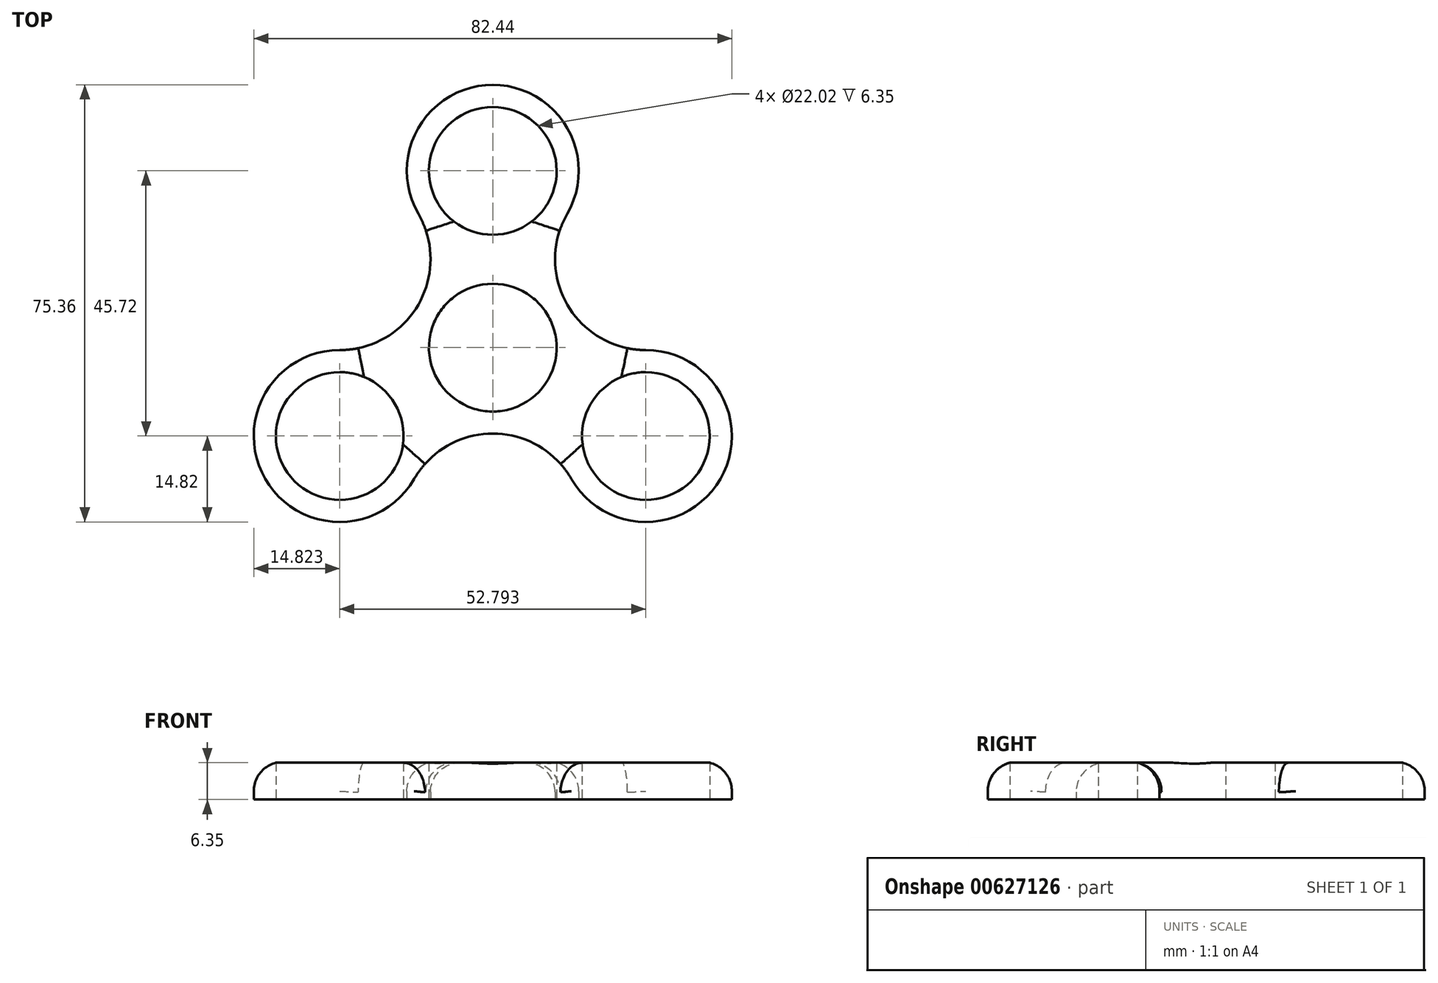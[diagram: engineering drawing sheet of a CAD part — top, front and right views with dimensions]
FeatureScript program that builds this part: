
annotation { "Feature Type Name" : "Feature", "Feature Type Description" : "" }
export const myFeature = defineFeature(function(context is Context, id is Id, definition is map)
    precondition{}
    {
        {
            var Q0;
            Q0=qCreatedBy(makeId("Top.planeOp"),FACE);
            var sketch = newSketch(context, id + "F0", { "sketchPlane" : qUnion([Q0])});
            skCircle(sketch, "E0", {"center": v(0, 0) * mm, "radius": 11.01 * mm});
            skCircle(sketch, "E1", {"center": v(0, 0) * mm, "radius": 14.82 * mm});
            skLineSegment(sketch, "E2", {"start": v(0, 0) * mm, "end": v(0, 30.48) * mm});
            skLineSegment(sketch, "E3", {"start": v(0, 0) * mm, "end": v(26.4, -15.24) * mm});
            skLineSegment(sketch, "E4", {"start": v(0, 0) * mm, "end": v(-26.4, -15.24) * mm});
            skCircle(sketch, "E5", {"center": v(-26.4, -15.24) * mm, "radius": 11.01 * mm});
            skCircle(sketch, "E6", {"center": v(26.4, -15.24) * mm, "radius": 11.01 * mm});
            skCircle(sketch, "E7", {"center": v(0, 30.48) * mm, "radius": 11.01 * mm});
            skCircle(sketch, "E8", {"center": v(0, 30.48) * mm, "radius": 14.82 * mm});
            skCircle(sketch, "E9", {"center": v(26.4, -15.24) * mm, "radius": 14.82 * mm});
            skCircle(sketch, "E10", {"center": v(-26.4, -15.24) * mm, "radius": 14.82 * mm});
            skArc(sketch, "E11", {"start": v(-26.4, -0.42) * mm, "mid": v(-12.84, 7.41) * mm, "end": v(-12.84, 23.07) * mm});
            skArc(sketch, "E12", {"start": v(12.84, 23.07) * mm, "mid": v(12.84, 7.41) * mm, "end": v(26.4, -0.42) * mm});
            skArc(sketch, "E13", {"start": v(13.56, -22.65) * mm, "mid": v(0, -14.82) * mm, "end": v(-13.56, -22.65) * mm});
            skSolve(sketch);
        }
        {
            var Q0;
            Q0 = qSketchRegion(id + "F0", true);
            var Q1;
            {var subQ0=sQuery(id+"F0.wireOp",EDGE,"E4");var subQ1=sQuery(id+"F0.wireOp",EDGE,"E0");var subQ2=makeQuery(id+"F0.imprint","INTERSECT",VERTEX,{"derivedFrom":[subQ1,subQ0]});Q1=makeQuery(id+"F0.imprint","IMPRINT",FACE,{"disambiguationData":[TD([[makeQuery(id+"F0.imprint","IMPRINT",EDGE,{"disambiguationData":[TD([[subQ2,1.0]])],"derivedFrom":subQ1}),-1.0]])]});}
            var Q2;
            {var subQ0=sQuery(id+"F0.wireOp",EDGE,"E4");var subQ1=sQuery(id+"F0.wireOp",EDGE,"E0");var subQ2=makeQuery(id+"F0.imprint","INTERSECT",VERTEX,{"derivedFrom":[subQ1,subQ0]});Q2=makeQuery(id+"F0.imprint","IMPRINT",FACE,{"disambiguationData":[TD([[makeQuery(id+"F0.imprint","IMPRINT",EDGE,{"disambiguationData":[TD([[subQ2,-1.0]])],"derivedFrom":subQ1}),-1.0]])]});}
            var Q3;
            {var subQ0=sQuery(id+"F0.wireOp",EDGE,"E2");var subQ1=sQuery(id+"F0.wireOp",EDGE,"E0");var subQ2=makeQuery(id+"F0.imprint","INTERSECT",VERTEX,{"derivedFrom":[subQ1,subQ0]});Q3=makeQuery(id+"F0.imprint","IMPRINT",FACE,{"disambiguationData":[TD([[makeQuery(id+"F0.imprint","IMPRINT",EDGE,{"disambiguationData":[TD([[subQ2,1.0]])],"derivedFrom":subQ1}),-1.0]])]});}
            extrude(context, id + "F1", {"entities" : qUnion([Q0, Q1, Q2, Q3]), "depth" : 6.35 * mm, "offsetDistance" : 25.4 * mm});
        }
        {
            var Q0;
            Q0=makeQuery(id+"F1.opExtrude","CAP_EDGE",EDGE,{"disambiguationData":[OSD([sQuery(id+"F0.wireOp",EDGE,"E10")])],"isStart":false});
            var Q1;
            Q1=makeQuery(id+"F1.opExtrude","CAP_EDGE",EDGE,{"disambiguationData":[OSD([sQuery(id+"F0.wireOp",EDGE,"E13")])],"isStart":false});
            fillet(context, id + "F2", {"entities" : qUnion([Q0, Q1]), "radius" : 5.08 * mm, "tangentPropagation" : true, "allowEdgeOverflow" : false});
        }
    });
